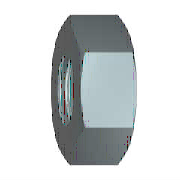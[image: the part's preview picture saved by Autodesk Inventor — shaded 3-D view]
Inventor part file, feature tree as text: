
AUTODESK INVENTOR PART (.ipt)
format: ipt  version: 2020 (Build 240168000, 168)  size: 165,376 bytes
history: native  units: mm (DEFAULTED — no unit token found)
features: sketch x3, extrude x1, chamfer x1, hole x1, other x1, plane x1
ambient origin geometry x7: Origin, YZ Plane, XZ Plane, X Axis, Y Axis, Z Axis, Center Point
bodies: Solid1 (feature_tree)
feature tree (8):
  extrude  "Körper"  Depth=2.4mm
  chamfer  "Fase1"  Angle=30.0deg  [1 undecoded]
  hole  "Gewinde"  [1 undecoded]
  other  "Work Axis1"
  plane  "Work Plane1"
  sketch  "Skizze1"  dims[d0=6.350853mm d1=2.4mm]
  sketch  "Skizze2"  dims[d2=0.0mm]
  sketch  "Skizze3"  dims[d3=30.0deg d4=30.0deg d5=4.6mm d6=4.6mm d7=90.0deg d25=2.459mm d26=6.0mm d27=4.0mm d28=2.0mm d29=14.3117mm d30=8.0mm d31=20.594885mm d8=0.270633mm d9=30.0deg d10=0.270633mm d11=30.0deg d13=0.0mm d14=0.0mm d39=0.0mm d40=0.270633mm d41=0.270633mm d42=0.0mm]
note: 2 required parameter values undecoded (feature->parameter linkage not recoverable at this tier; creation-order binding heuristic only, values carry confidence <= 0.55)
